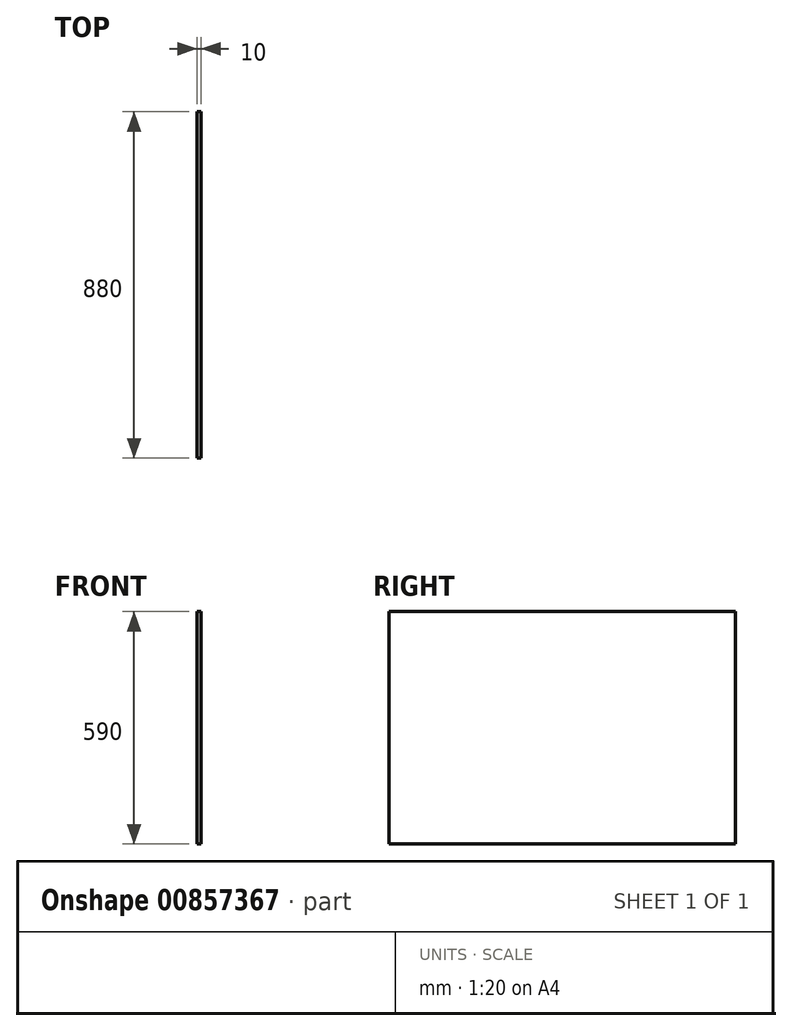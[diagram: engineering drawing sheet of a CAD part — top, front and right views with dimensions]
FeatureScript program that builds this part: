
annotation { "Feature Type Name" : "Feature", "Feature Type Description" : "" }
export const myFeature = defineFeature(function(context is Context, id is Id, definition is map)
    precondition{}
    {
        {
            var Q0;
            Q0=qCreatedBy(makeId("Right.planeOp"),FACE);
            var sketch = newSketch(context, id + "F0", { "sketchPlane" : qUnion([Q0])});
            skLineSegment(sketch, "E0.bottom", {"start": v(-400, 295) * mm, "end": v(480, 295) * mm});
            skLineSegment(sketch, "E0.top", {"start": v(-400, -295) * mm, "end": v(480, -295) * mm});
            skLineSegment(sketch, "E0.left", {"start": v(-400, 295) * mm, "end": v(-400, -295) * mm});
            skLineSegment(sketch, "E0.right", {"start": v(480, 295) * mm, "end": v(480, -295) * mm});
            skSolve(sketch);
        }
        {
            var Q0;
            Q0=makeQuery(id+"F0.imprint","IMPRINT",FACE,{"disambiguationData":[TD([[makeQuery(id+"F0.imprint","IMPRINT",EDGE,{"derivedFrom":sQuery(id+"F0.wireOp",EDGE,"E0.bottom")}),-1.0]])]});
            extrude(context, id + "F1", {"entities" : qUnion([Q0]), "depth" : 10 * mm, "offsetDistance" : 25 * mm});
        }
    });
